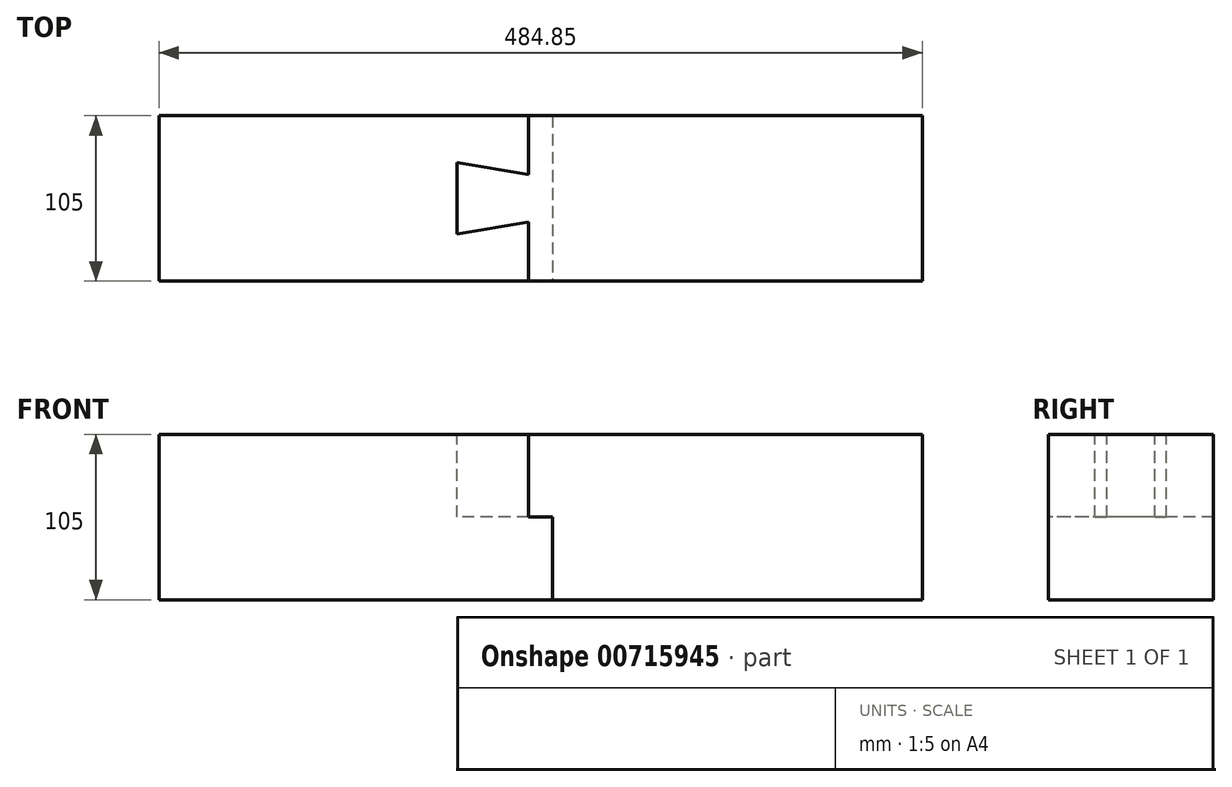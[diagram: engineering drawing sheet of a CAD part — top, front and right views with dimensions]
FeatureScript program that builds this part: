
annotation { "Feature Type Name" : "Feature", "Feature Type Description" : "" }
export const myFeature = defineFeature(function(context is Context, id is Id, definition is map)
    precondition{}
    {
        {
            var Q0;
            Q0=qCreatedBy(makeId("Top.planeOp"),FACE);
            var sketch = newSketch(context, id + "F0", { "sketchPlane" : qUnion([Q0])});
            skLineSegment(sketch, "E0.bottom", {"start": v(0, 52.5) * mm, "end": v(250, 52.5) * mm});
            skLineSegment(sketch, "E0.top", {"start": v(0, -52.5) * mm, "end": v(250, -52.5) * mm});
            skLineSegment(sketch, "E0.left", {"start": v(0, 52.5) * mm, "end": v(0, -52.5) * mm});
            skLineSegment(sketch, "E0.right", {"start": v(250, 52.5) * mm, "end": v(250, -52.5) * mm});
            skSolve(sketch);
        }
        {
            var Q0;
            Q0=makeQuery(id+"F0.imprint","IMPRINT",FACE,{"disambiguationData":[TD([[makeQuery(id+"F0.imprint","IMPRINT",EDGE,{"derivedFrom":sQuery(id+"F0.wireOp",EDGE,"E0.bottom")}),-1.0]])]});
            extrude(context, id + "F1", {"entities" : qUnion([Q0]), "depth" : 105 * mm, "offsetDistance" : 25 * mm, "symmetric" : true});
        }
        {
            var Q0;
            Q0=makeQuery(id+"F1.opExtrude","SWEPT_FACE",FACE,{"disambiguationData":[OSD([sQuery(id+"F0.wireOp",EDGE,"E0.left")])]});
            var sketch = newSketch(context, id + "F2", { "sketchPlane" : qUnion([Q0])});
            skLineSegment(sketch, "E1.bottom", {"start": v(-52.5, -52.5) * mm, "end": v(52.5, -52.5) * mm});
            skLineSegment(sketch, "E1.top", {"start": v(-52.5, 0) * mm, "end": v(52.5, 0) * mm});
            skLineSegment(sketch, "E1.left", {"start": v(-52.5, -52.5) * mm, "end": v(-52.5, 0) * mm});
            skLineSegment(sketch, "E1.right", {"start": v(52.5, -52.5) * mm, "end": v(52.5, 0) * mm});
            skSolve(sketch);
        }
        {
            var Q0;
            Q0=makeQuery(id+"F2.imprint","IMPRINT",FACE,{"disambiguationData":[TD([[makeQuery(id+"F2.imprint","IMPRINT",EDGE,{"derivedFrom":sQuery(id+"F2.wireOp",EDGE,"E1.bottom")}),1.0]])]});
            extrude(context, id + "F3", {"entities" : qUnion([Q0]), "operationType" : NewBodyOperationType.REMOVE, "oppositeDirection" : true, "depth" : 15.15 * mm, "offsetDistance" : 25 * mm});
        }
        {
            var Q0;
            Q0=makeQuery(id+"F1.opExtrude","CAP_FACE",FACE,{"disambiguationData":[OSD([sQuery(id+"F0.wireOp",EDGE,"E0.bottom"),sQuery(id+"F0.wireOp",EDGE,"E0.top"),sQuery(id+"F0.wireOp",EDGE,"E0.left"),sQuery(id+"F0.wireOp",EDGE,"E0.right")])],"isStart":false});
            var sketch = newSketch(context, id + "F4", { "sketchPlane" : qUnion([Q0])});
            skLineSegment(sketch, "E2", {"start": v(0, 15.15) * mm, "end": v(-45.45, 22.73) * mm});
            skLineSegment(sketch, "E3", {"start": v(-45.45, 22.73) * mm, "end": v(-45.45, -22.73) * mm});
            skLineSegment(sketch, "E4", {"start": v(-45.45, -22.73) * mm, "end": v(0, -15.15) * mm});
            skLineSegment(sketch, "E5", {"start": v(0, 0) * mm, "end": v(-45.45, 0) * mm, "construction": true});
            skSolve(sketch);
        }
        {
            var Q0;
            {var subQ0=sQuery(id+"F4.wireOp",EDGE,"E2");Q0=makeQuery(id+"F4.imprint","IMPRINT",FACE,{"disambiguationData":[TD([[makeQuery(id+"F4.imprint","IMPRINT",EDGE,{"derivedFrom":subQ0}),1.0]])]});}
            var Q1;
            Q1=makeQuery(id+"F3.boolean.opBoolean","COPY",FACE,{"derivedFrom":makeQuery(id+"F3.opExtrude","SWEPT_FACE",FACE,{"disambiguationData":[OSD([sQuery(id+"F2.wireOp",EDGE,"E1.top")])]})});
            extrude(context, id + "F5", {"entities" : qUnion([Q0]), "operationType" : NewBodyOperationType.ADD, "endBound" : BoundingType.UP_TO_SURFACE, "oppositeDirection" : true, "depth" : 25 * mm, "endBoundEntityFace" : qUnion([Q1]), "offsetDistance" : 25 * mm});
        }
        {
            var Q0;
            Q0=qCreatedBy(makeId("Top.planeOp"),FACE);
            var sketch = newSketch(context, id + "F6", { "sketchPlane" : qUnion([Q0])});
            skLineSegment(sketch, "E6.0", {"start": v(15.15, 52.5) * mm, "end": v(15.15, -52.5) * mm});
            skLineSegment(sketch, "E7", {"start": v(15.15, 52.5) * mm, "end": v(-234.85, 52.5) * mm});
            skLineSegment(sketch, "E8", {"start": v(-234.85, 52.5) * mm, "end": v(-234.85, -52.5) * mm});
            skLineSegment(sketch, "E9", {"start": v(-234.85, -52.5) * mm, "end": v(15.15, -52.5) * mm});
            skSolve(sketch);
        }
        {
            var Q0;
            Q0=makeQuery(id+"F6.imprint","IMPRINT",FACE,{"disambiguationData":[TD([[makeQuery(id+"F6.imprint","IMPRINT",EDGE,{"derivedFrom":sQuery(id+"F6.wireOp",EDGE,"E6.0")}),-1.0]])]});
            var Q1;
            {var subQ0=sQuery(id+"F0.wireOp",EDGE,"E0.left");Q1=makeQuery(id+"F5.boolean.opBoolean","MERGE",FACE,{"derivedFrom":[makeQuery(id+"F1.opExtrude","CAP_FACE",FACE,{"disambiguationData":[OSD([sQuery(id+"F0.wireOp",EDGE,"E0.bottom"),sQuery(id+"F0.wireOp",EDGE,"E0.top"),subQ0,sQuery(id+"F0.wireOp",EDGE,"E0.right")])],"isStart":false}),makeQuery(id+"F5.opExtrude","CAP_FACE",FACE,{"disambiguationData":[OSD([subQ0,sQuery(id+"F4.wireOp",EDGE,"E2"),sQuery(id+"F4.wireOp",EDGE,"E3"),sQuery(id+"F4.wireOp",EDGE,"E4")])],"isStart":true})]});}
            var Q2;
            Q2=makeQuery(id+"F1.opExtrude","CAP_FACE",FACE,{"disambiguationData":[OSD([sQuery(id+"F0.wireOp",EDGE,"E0.bottom"),sQuery(id+"F0.wireOp",EDGE,"E0.top"),sQuery(id+"F0.wireOp",EDGE,"E0.left"),sQuery(id+"F0.wireOp",EDGE,"E0.right")])],"isStart":true});
            extrude(context, id + "F7", {"entities" : qUnion([Q0]), "endBound" : BoundingType.UP_TO_SURFACE, "depth" : 105 * mm, "endBoundEntityFace" : qUnion([Q1]), "offsetDistance" : 25 * mm, "hasSecondDirection" : true, "secondDirectionBound" : BoundingType.UP_TO_SURFACE, "secondDirectionOppositeDirection" : true, "secondDirectionDepth" : 25 * mm, "secondDirectionBoundEntityFace" : qUnion([Q2])});
        }
        {
            var Q0;
            Q0=makeQuery(id+"F1.opExtrude","SWEPT_BODY",BODY,{"disambiguationData":[OSD([sQuery(id+"F0.wireOp",EDGE,"E0.bottom"),sQuery(id+"F0.wireOp",EDGE,"E0.top"),sQuery(id+"F0.wireOp",EDGE,"E0.left"),sQuery(id+"F0.wireOp",EDGE,"E0.right")])]});
            var Q1;
            Q1=makeQuery(id+"F7.opExtrude","SWEPT_BODY",BODY,{"disambiguationData":[OSD([sQuery(id+"F6.wireOp",EDGE,"E6.0"),sQuery(id+"F6.wireOp",EDGE,"E7"),sQuery(id+"F6.wireOp",EDGE,"E8"),sQuery(id+"F6.wireOp",EDGE,"E9")])]});
            booleanBodies(context, id + "F8", {"operationType" : BooleanOperationType.SUBTRACTION, "tools" : qUnion([Q0]), "targets" : qUnion([Q1]), "keepTools" : true});
        }
    });
